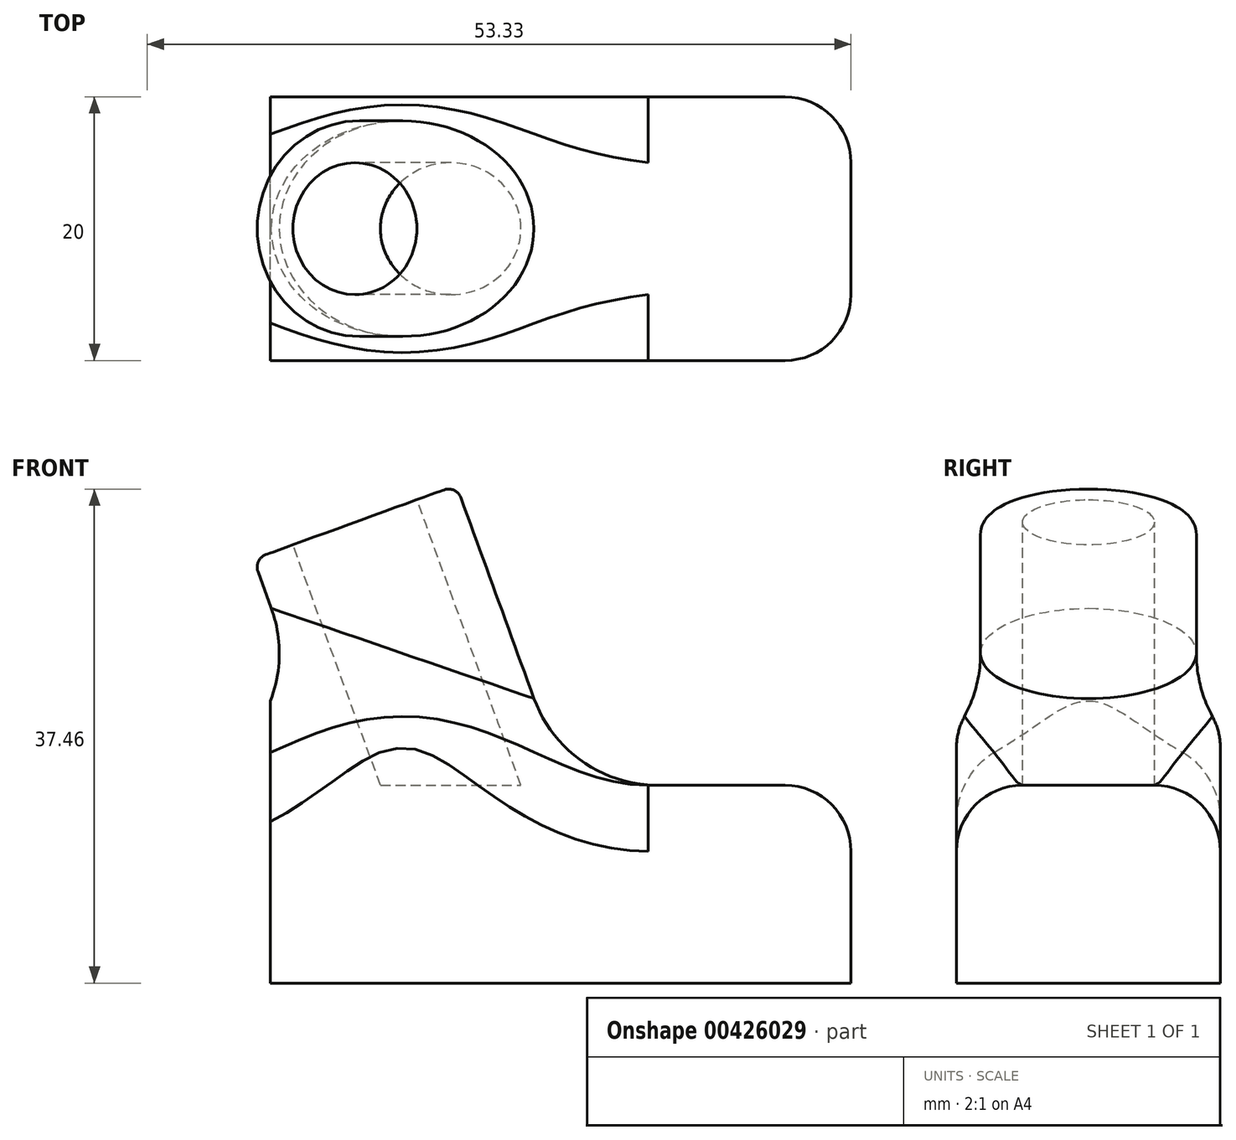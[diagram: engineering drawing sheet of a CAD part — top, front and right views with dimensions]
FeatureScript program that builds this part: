
annotation { "Feature Type Name" : "Feature", "Feature Type Description" : "" }
export const myFeature = defineFeature(function(context is Context, id is Id, definition is map)
    precondition{}
    {
        {
            var Q0;
            Q0=qCreatedBy(makeId("Front.planeOp"),FACE);
            var sketch = newSketch(context, id + "F0", { "sketchPlane" : qUnion([Q0])});
            skLineSegment(sketch, "E0", {"start": v(-9.37, 25.74) * mm, "end": v(0, 0) * mm});
            skLineSegment(sketch, "E1", {"start": v(-3.39, 0) * mm, "end": v(-12.36, 24.65) * mm});
            skLineSegment(sketch, "E2", {"start": v(-10.87, 44.48) * mm, "end": v(5.32, 0) * mm, "construction": true});
            skLineSegment(sketch, "E3", {"start": v(-9.37, 25.74) * mm, "end": v(-12.36, 24.65) * mm});
            skLineSegment(sketch, "E4", {"start": v(0, 0) * mm, "end": v(-2.97, -1.08) * mm});
            skLineSegment(sketch, "E5", {"start": v(-2.97, -1.08) * mm, "end": v(-3.39, 0) * mm});
            skPoint(sketch, "E6.orphan", {"position": v(-12.75, 25.74) * mm});
            skSolve(sketch);
        }
        {
            var Q0;
            Q0=makeQuery(id+"F0.imprint","IMPRINT",FACE,{"disambiguationData":[TD([[makeQuery(id+"F0.imprint","IMPRINT",EDGE,{"derivedFrom":sQuery(id+"F0.wireOp",EDGE,"E0")}),-1.0]])]});
            var Q1;
            Q1=sQuery(id+"F0.wireOp",EDGE,"E2");
            revolve(context, id + "F1", {"surfaceOperationType" : NewSurfaceOperationType.NEW, "entities" : qUnion([Q0]), "axis" : qUnion([Q1]), "revolveType" : RevolveType.FULL});
        }
        {
            var Q0;
            Q0=qCreatedBy(makeId("Front.planeOp"),FACE);
            var sketch = newSketch(context, id + "F2", { "sketchPlane" : qUnion([Q0])});
            skLineSegment(sketch, "E7.bottom", {"start": v(-11.07, -7.5) * mm, "end": v(32.93, -7.5) * mm});
            skLineSegment(sketch, "E7.top", {"start": v(-11.07, 7.5) * mm, "end": v(32.93, 7.5) * mm});
            skLineSegment(sketch, "E7.left", {"start": v(-11.07, -7.5) * mm, "end": v(-11.07, 7.5) * mm});
            skLineSegment(sketch, "E7.right", {"start": v(32.93, -7.5) * mm, "end": v(32.93, 7.5) * mm});
            skPoint(sketch, "E7.middle", {"position": v(10.93, 0) * mm});
            skSolve(sketch);
        }
        {
            var Q0;
            Q0=makeQuery(id+"F2.imprint","IMPRINT",FACE,{"disambiguationData":[TD([[makeQuery(id+"F2.imprint","IMPRINT",EDGE,{"derivedFrom":sQuery(id+"F2.wireOp",EDGE,"E7.bottom")}),1.0]])]});
            extrude(context, id + "F3", {"entities" : qUnion([Q0]), "operationType" : NewBodyOperationType.ADD, "depth" : 10 * mm, "offsetDistance" : 25 * mm, "hasSecondDirection" : true, "secondDirectionOppositeDirection" : true, "secondDirectionDepth" : 10 * mm});
        }
        {
            var Q0;
            Q0=makeQuery(id+"F3.boolean.opBoolean","INTERSECT",EDGE,{"derivedFrom":[makeQuery(id+"F1.opRevolve","SWEPT_FACE",FACE,{"disambiguationData":[OSD([sQuery(id+"F0.wireOp",EDGE,"E1")])]}),makeQuery(id+"F3.opExtrude","SWEPT_FACE",FACE,{"disambiguationData":[OSD([sQuery(id+"F2.wireOp",EDGE,"E7.top")])]})]});
            fillet(context, id + "F4", {"entities" : qUnion([Q0]), "radius" : 10 * mm, "tangentPropagation" : true, "allowEdgeOverflow" : false});
        }
        {
            var Q0;
            Q0=makeQuery(id+"F3.opExtrude","SWEPT_EDGE",EDGE,{"disambiguationData":[OSD([sQuery(id+"F2.wireOp",EDGE,"E7.top"),sQuery(id+"F2.wireOp",EDGE,"E7.right")])]});
            fillet(context, id + "F5", {"entities" : qUnion([Q0]), "radius" : 5 * mm, "tangentPropagation" : true, "allowEdgeOverflow" : false});
        }
        {
            var Q0;
            Q0=makeQuery(id+"F1.opRevolve","SWEPT_EDGE",EDGE,{"disambiguationData":[OSD([sQuery(id+"F0.wireOp",EDGE,"E1"),sQuery(id+"F0.wireOp",EDGE,"E3")])]});
            fillet(context, id + "F6", {"entities" : qUnion([Q0]), "radius" : 1 * mm, "tangentPropagation" : true, "allowEdgeOverflow" : false});
        }
        {
            var Q0;
            Q0=makeQuery(id+"F3.opExtrude","CAP_EDGE",EDGE,{"disambiguationData":[OSD([sQuery(id+"F2.wireOp",EDGE,"E7.top")])],"isStart":false});
            var Q1;
            Q1=makeQuery(id+"F3.opExtrude","CAP_EDGE",EDGE,{"disambiguationData":[OSD([sQuery(id+"F2.wireOp",EDGE,"E7.top")])],"isStart":true});
            fillet(context, id + "F7", {"entities" : qUnion([Q0, Q1]), "radius" : 5 * mm, "tangentPropagation" : true, "allowEdgeOverflow" : false});
        }
    });
